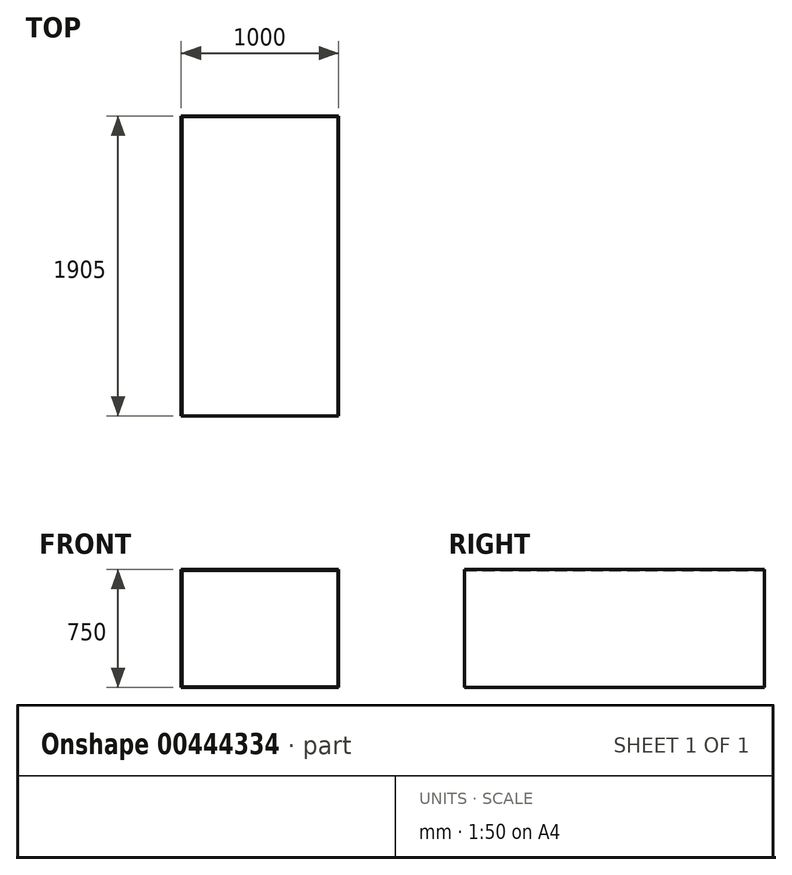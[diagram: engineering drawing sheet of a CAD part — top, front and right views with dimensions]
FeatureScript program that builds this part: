
annotation { "Feature Type Name" : "Feature", "Feature Type Description" : "" }
export const myFeature = defineFeature(function(context is Context, id is Id, definition is map)
    precondition{}
    {
        {
            var Q0;
            Q0=qCreatedBy(makeId("Front.planeOp"),FACE);
            var sketch = newSketch(context, id + "F0", { "sketchPlane" : qUnion([Q0])});
            skLineSegment(sketch, "E0.bottom", {"start": v(500, -375) * mm, "end": v(-500, -375) * mm});
            skLineSegment(sketch, "E0.top", {"start": v(500, 375) * mm, "end": v(-500, 375) * mm});
            skLineSegment(sketch, "E0.left", {"start": v(500, -375) * mm, "end": v(500, 375) * mm});
            skLineSegment(sketch, "E0.right", {"start": v(-500, -375) * mm, "end": v(-500, 375) * mm});
            skPoint(sketch, "E0.middle", {"position": v(0, 0) * mm});
            skSolve(sketch);
        }
        {
            var Q0;
            Q0 = qSketchRegion(id + "F0", true);
            extrude(context, id + "F1", {"entities" : qUnion([Q0]), "depth" : 5 * mm});
        }
        {
            var Q0;
            Q0=makeQuery(id+"F1.opExtrude","CAP_FACE",FACE,{"disambiguationData":[OSD([sQuery(id+"F0.wireOp",EDGE,"E0.bottom"),sQuery(id+"F0.wireOp",EDGE,"E0.top"),sQuery(id+"F0.wireOp",EDGE,"E0.left"),sQuery(id+"F0.wireOp",EDGE,"E0.right")])],"isStart":false});
            var sketch = newSketch(context, id + "F2", { "sketchPlane" : qUnion([Q0])});
            skLineSegment(sketch, "E1.bottom", {"start": v(-500, 375) * mm, "end": v(-495, 375) * mm});
            skLineSegment(sketch, "E1.top", {"start": v(-500, -375) * mm, "end": v(-495, -375) * mm});
            skLineSegment(sketch, "E1.left", {"start": v(-500, 375) * mm, "end": v(-500, -375) * mm});
            skLineSegment(sketch, "E1.right", {"start": v(-495, 375) * mm, "end": v(-495, -375) * mm});
            skLineSegment(sketch, "E2", {"start": v(0, 375) * mm, "end": v(0, -375) * mm, "construction": true});
            skLineSegment(sketch, "E3.MirrorCS", {"start": v(500, 375) * mm, "end": v(495, 375) * mm});
            skLineSegment(sketch, "E4.MirrorCS", {"start": v(500, 375) * mm, "end": v(500, -375) * mm});
            skLineSegment(sketch, "E5.MirrorCS", {"start": v(495, 375) * mm, "end": v(495, -375) * mm});
            skLineSegment(sketch, "E6.MirrorCS", {"start": v(500, -375) * mm, "end": v(495, -375) * mm});
            skSolve(sketch);
        }
        {
            var Q0;
            Q0 = qSketchRegion(id + "F2", true);
            extrude(context, id + "F3", {"entities" : qUnion([Q0]), "operationType" : NewBodyOperationType.ADD, "depth" : 1900 * mm});
        }
        {
            var Q0;
            Q0=makeQuery(id+"F1.opExtrude","CAP_FACE",FACE,{"disambiguationData":[OSD([sQuery(id+"F0.wireOp",EDGE,"E0.bottom"),sQuery(id+"F0.wireOp",EDGE,"E0.top"),sQuery(id+"F0.wireOp",EDGE,"E0.left"),sQuery(id+"F0.wireOp",EDGE,"E0.right")])],"isStart":false});
            var sketch = newSketch(context, id + "F4", { "sketchPlane" : qUnion([Q0])});
            skLineSegment(sketch, "E7", {"start": v(0, 375) * mm, "end": v(0, -375) * mm, "construction": true});
            skSolve(sketch);
        }
        {
            var Q0;
            Q0 = qSketchRegion(id + "F2", true);
            extrude(context, id + "F5", {"entities" : qUnion([Q0]), "operationType" : NewBodyOperationType.ADD, "depth" : 1900 * mm});
        }
        {
            var Q0;
            Q0=makeQuery(id+"F4.imprint","IMPRINT",FACE,{"disambiguationData":[TD([[makeQuery(id+"F4.imprint","IMPRINT",EDGE,{"derivedFrom":makeQuery(id+"F1.opExtrude","CAP_EDGE",EDGE,{"disambiguationData":[OSD([sQuery(id+"F0.wireOp",EDGE,"E0.bottom")])],"isStart":false})}),-1.0]])]});
            var sketch = newSketch(context, id + "F6", { "sketchPlane" : qUnion([Q0])});
            skLineSegment(sketch, "E8", {"start": v(-494.97, 374.95) * mm, "end": v(-494.97, 369.95) * mm});
            skLineSegment(sketch, "E9", {"start": v(-494.97, 369.95) * mm, "end": v(495.03, 369.95) * mm});
            skLineSegment(sketch, "E10", {"start": v(495.03, 369.95) * mm, "end": v(495.03, 374.95) * mm});
            skLineSegment(sketch, "E11", {"start": v(495.03, 374.95) * mm, "end": v(-494.97, 374.95) * mm});
            skLineSegment(sketch, "E12", {"start": v(-496.58, 0) * mm, "end": v(509.22, 0) * mm, "construction": true});
            skLineSegment(sketch, "E13.MirrorCS", {"start": v(495.02, -374.96) * mm, "end": v(-494.98, -374.95) * mm});
            skLineSegment(sketch, "E14.MirrorCS", {"start": v(495.02, -369.96) * mm, "end": v(495.02, -374.96) * mm});
            skLineSegment(sketch, "E15.MirrorCS", {"start": v(-494.98, -369.95) * mm, "end": v(495.02, -369.96) * mm});
            skLineSegment(sketch, "E16.MirrorCS", {"start": v(-494.98, -374.95) * mm, "end": v(-494.98, -369.95) * mm});
            skSolve(sketch);
        }
        {
            var Q0;
            Q0 = qSketchRegion(id + "F6", true);
            extrude(context, id + "F7", {"entities" : qUnion([Q0]), "depth" : 1900 * mm});
        }
        {
            var Q0;
            Q0 = qSketchRegion(id + "F6", true);
            extrude(context, id + "F8", {"entities" : qUnion([Q0]), "depth" : 1900 * mm});
        }
    });
